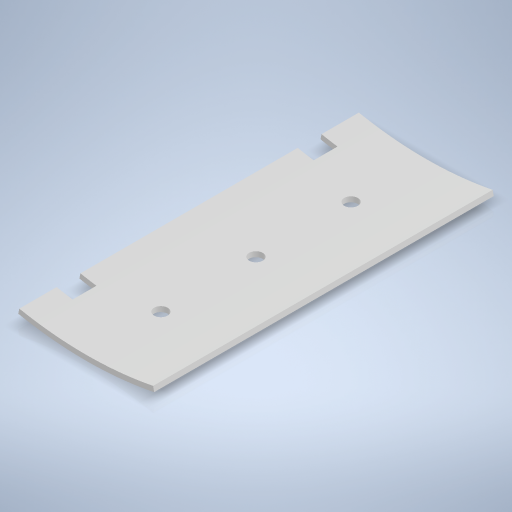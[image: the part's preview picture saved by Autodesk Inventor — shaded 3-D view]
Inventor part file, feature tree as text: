
AUTODESK INVENTOR PART (.ipt)
format: ipt  version: 2024 (Build 280153000, 153)  size: 267,776 bytes
history: native  units: mm
features: sketch x3, extrude x2, plane x1, hole x1
ambient origin geometry x8: Origin, YZ Plane, XZ Plane, XY Plane, X Axis, Y Axis, Z Axis, Center Point
bodies: Volumenkörper1 (feature_tree)
feature tree (7):
  extrude  "Extrusion1"  Depth=101.0mm
  plane  "Arbeitsebene1"
  hole  "Bohrung1"  [1 undecoded]
  extrude  "Extrusion2"  [1 undecoded]
  sketch  "Skizze1"  dims[d0=2.0mm d1=101.0mm]
  sketch  "Skizze2"  dims[d2=40.0mm d3=35.0mm]
  sketch  "Skizze3"  dims[d4=100.0mm d5=0.0mm d6=-66.0mm d7=22.0mm d8=22.0mm d9=28.0mm d10=4.0mm d11=6.0mm d12=4.0mm d13=2.0mm d14=90.0deg d15=8.0mm d16=20.594885mm d17=5.0mm d18=7.0mm d19=11.0mm d20=5.0mm d21=7.0mm d22=11.0mm d23=0.0mm d24=0.0mm]
note: 2 required parameter values undecoded (feature->parameter linkage not recoverable at this tier; creation-order binding heuristic only, values carry confidence <= 0.55)
